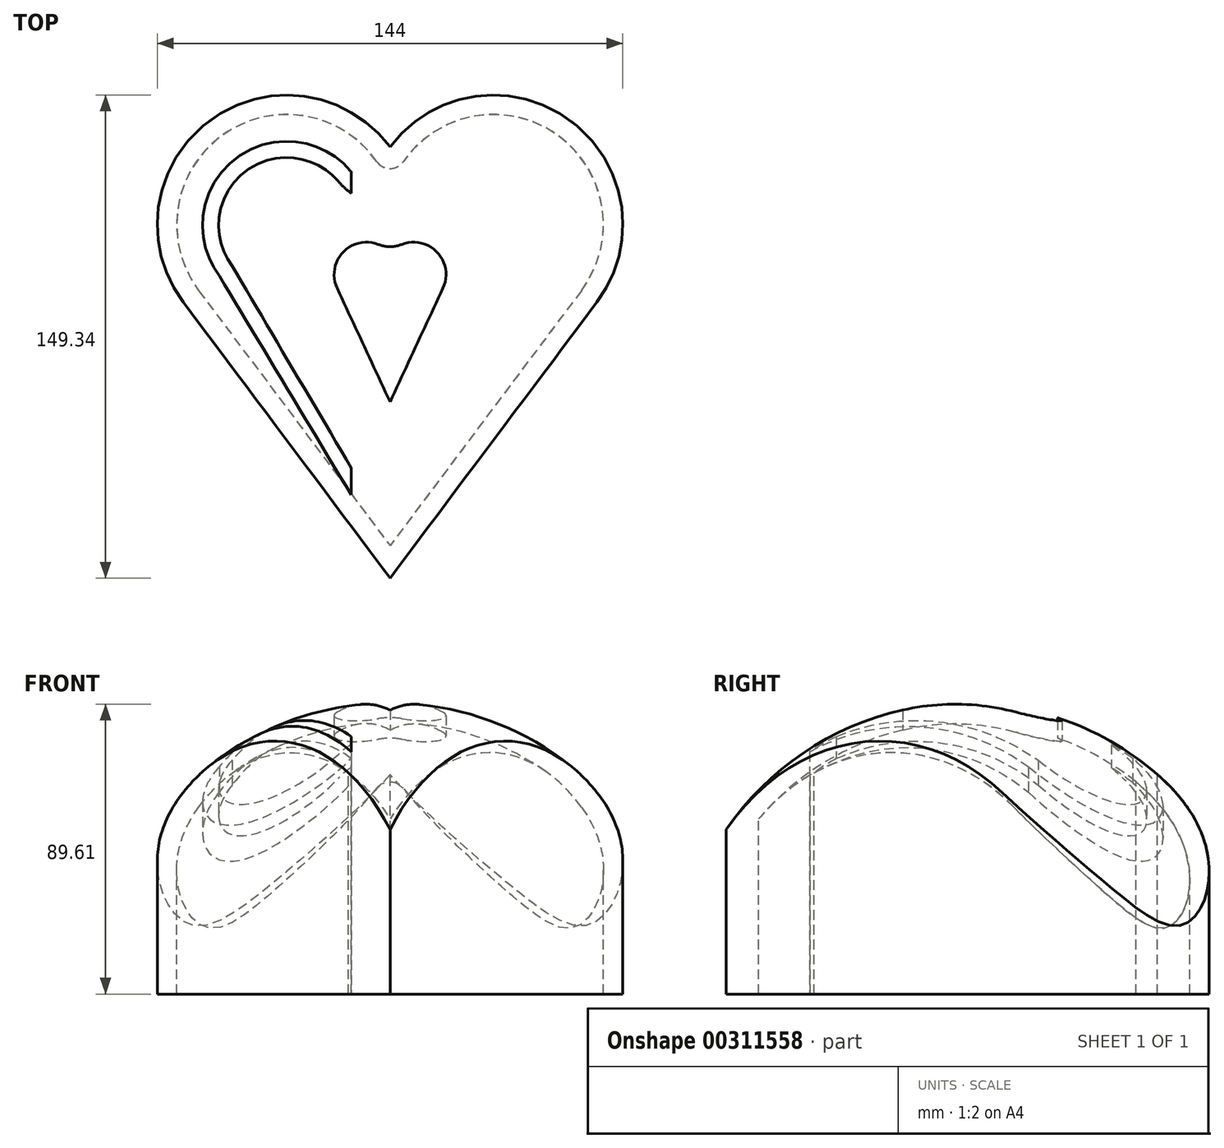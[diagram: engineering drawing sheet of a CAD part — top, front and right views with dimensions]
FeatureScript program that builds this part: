
annotation { "Feature Type Name" : "Feature", "Feature Type Description" : "" }
export const myFeature = defineFeature(function(context is Context, id is Id, definition is map)
    precondition{}
    {
        {
            var Q0;
            Q0=qCreatedBy(makeId("Top.planeOp"),FACE);
            var sketch = newSketch(context, id + "F0", { "sketchPlane" : qUnion([Q0])});
            skArc(sketch, "E0", {"start": v(0, -90) * mm, "mid": v(90, 0) * mm, "end": v(0, 90) * mm});
            skLineSegment(sketch, "E1", {"start": v(0, -90) * mm, "end": v(0, 90) * mm});
            skSolve(sketch);
        }
        {
            var Q0;
            Q0=qCreatedBy(makeId("Top.planeOp"),FACE);
            var sketch = newSketch(context, id + "F1", { "sketchPlane" : qUnion([Q0])});
            skLineSegment(sketch, "E2", {"start": v(0, -74.22) * mm, "end": v(-64, 11.12) * mm});
            skArc(sketch, "E3", {"start": v(0, 59.12) * mm, "mid": v(-56, 67.12) * mm, "end": v(-64, 11.12) * mm});
            skArc(sketch, "E4.MirrorCS", {"start": v(0, 59.12) * mm, "mid": v(56, 67.12) * mm, "end": v(64, 11.12) * mm});
            skLineSegment(sketch, "E5.MirrorCS", {"start": v(0, -74.22) * mm, "end": v(64, 11.12) * mm});
            skPoint(sketch, "E6.orphan", {"position": v(0, 11.12) * mm});
            skCircle(sketch, "E7", {"center": v(0, 0) * mm, "radius": 132.96 * mm});
            skSolve(sketch);
        }
        {
            var Q0;
            Q0=makeQuery(id+"F0.imprint","IMPRINT",FACE,{"disambiguationData":[TD([[makeQuery(id+"F0.imprint","IMPRINT",EDGE,{"derivedFrom":sQuery(id+"F0.wireOp",EDGE,"E0")}),1.0]])]});
            var Q1;
            Q1=sQuery(id+"F0.wireOp",EDGE,"E1");
            revolve(context, id + "F2", {"entities" : qUnion([Q0]), "axis" : qUnion([Q1]), "revolveType" : RevolveType.FULL});
        }
        {
            var Q0;
            Q0=makeQuery(id+"F1.imprint","IMPRINT",FACE,{"disambiguationData":[TD([[makeQuery(id+"F1.imprint","IMPRINT",EDGE,{"derivedFrom":sQuery(id+"F1.wireOp",EDGE,"E2")}),1.0]])]});
            extrude(context, id + "F3", {"entities" : qUnion([Q0]), "operationType" : NewBodyOperationType.REMOVE, "endBound" : BoundingType.SYMMETRIC, "oppositeDirection" : true, "depth" : 255 * mm});
        }
        {
            var Q0;
            Q0=qCreatedBy(makeId("Right.planeOp"),FACE);
            var sketch = newSketch(context, id + "F4", { "sketchPlane" : qUnion([Q0])});
            skLineSegment(sketch, "E8.bottom", {"start": v(92.34, 0) * mm, "end": v(-99.26, 0) * mm});
            skLineSegment(sketch, "E8.top", {"start": v(92.34, -98.37) * mm, "end": v(-99.26, -98.37) * mm});
            skLineSegment(sketch, "E8.left", {"start": v(92.34, 0) * mm, "end": v(92.34, -98.37) * mm});
            skLineSegment(sketch, "E8.right", {"start": v(-99.26, 0) * mm, "end": v(-99.26, -98.37) * mm});
            skSolve(sketch);
        }
        {
            var Q0;
            Q0=makeQuery(id+"F4.imprint","IMPRINT",FACE,{"disambiguationData":[TD([[makeQuery(id+"F4.imprint","IMPRINT",EDGE,{"derivedFrom":sQuery(id+"F4.wireOp",EDGE,"E8.bottom")}),1.0]])]});
            extrude(context, id + "F5", {"entities" : qUnion([Q0]), "operationType" : NewBodyOperationType.REMOVE, "endBound" : BoundingType.SYMMETRIC, "oppositeDirection" : true, "depth" : 202.6 * mm});
        }
        {
            var Q0;
            Q0=makeQuery(id+"F5.boolean.opBoolean","COPY",FACE,{"derivedFrom":makeQuery(id+"F5.opExtrude","SWEPT_FACE",FACE,{"disambiguationData":[OSD([sQuery(id+"F4.wireOp",EDGE,"E8.bottom")])]})});
            shell(context, id + "F6", {"entities" : qUnion([Q0]), "thickness" : 6 * mm});
        }
        {
            var Q0;
            Q0=qCreatedBy(makeId("Top.planeOp"),FACE);
            var sketch = newSketch(context, id + "F7", { "sketchPlane" : qUnion([Q0])});
            skPoint(sketch, "E9.visualSharp", {"position": v(0, 46.32) * mm});
            skArc(sketch, "E10.0", {"start": v(-12.2, 51.67) * mm, "mid": v(-48.23, 55.14) * mm, "end": v(-52.8, 19.23) * mm});
            skLineSegment(sketch, "E10.1", {"start": v(-12, -48.5) * mm, "end": v(-52.8, 19.23) * mm});
            skArc(sketch, "E10.2", {"start": v(-12.2, 51.67) * mm, "mid": v(-12.1, 51.56) * mm, "end": v(-12, 51.45) * mm});
            skArc(sketch, "E10.3", {"start": v(12.2, 51.67) * mm, "mid": v(48.23, 55.14) * mm, "end": v(52.8, 19.23) * mm});
            skLineSegment(sketch, "E10.4", {"start": v(12, -48.5) * mm, "end": v(52.8, 19.23) * mm});
            skArc(sketch, "E11.0", {"start": v(16, 48.43) * mm, "mid": v(45.1, 51.24) * mm, "end": v(48.8, 22.23) * mm});
            skArc(sketch, "E11.1", {"start": v(-16, 48.43) * mm, "mid": v(-14.12, 46.49) * mm, "end": v(-12, 44.8) * mm});
            skArc(sketch, "E11.2", {"start": v(-16, 48.43) * mm, "mid": v(-45.1, 51.24) * mm, "end": v(-48.8, 22.23) * mm});
            skLineSegment(sketch, "E12.trimOffspring", {"start": v(-12, -40.17) * mm, "end": v(-48.8, 22.23) * mm});
            skLineSegment(sketch, "E13.trimOffspring", {"start": v(12, -40.17) * mm, "end": v(48.8, 22.23) * mm});
            skLineSegment(sketch, "E14", {"start": v(-12, -48.5) * mm, "end": v(-12, -40.17) * mm});
            skLineSegment(sketch, "E15.MirrorCS", {"start": v(12, -48.5) * mm, "end": v(12, -40.17) * mm});
            skPoint(sketch, "E16.orphan", {"position": v(-12, -28.45) * mm});
            skPoint(sketch, "E17.orphan", {"position": v(12, -28.45) * mm});
            skPoint(sketch, "E18.orphan", {"position": v(0, -68.42) * mm});
            skPoint(sketch, "E19.orphan", {"position": v(-12, -53.75) * mm});
            skPoint(sketch, "E20.orphan", {"position": v(12, -53.75) * mm});
            skLineSegment(sketch, "E21", {"start": v(-12, 44.8) * mm, "end": v(-12, 51.45) * mm});
            skLineSegment(sketch, "E22.MirrorCS", {"start": v(12, 44.8) * mm, "end": v(12, 51.45) * mm});
            skPoint(sketch, "E23.orphan", {"position": v(-12, 35.9) * mm});
            skArc(sketch, "E24.trimOffspring", {"start": v(12, 44.8) * mm, "mid": v(14.12, 46.49) * mm, "end": v(16, 48.43) * mm});
            skArc(sketch, "E25.trimOffspring", {"start": v(12, 51.45) * mm, "mid": v(12.1, 51.56) * mm, "end": v(12.2, 51.67) * mm});
            skPoint(sketch, "E26.orphan", {"position": v(-12, 54.73) * mm});
            skPoint(sketch, "E27.orphan", {"position": v(12, 54.73) * mm});
            skPoint(sketch, "E28.orphan", {"position": v(12, 35.9) * mm});
            skSolve(sketch);
        }
        {
            var Q0;
            Q0=makeQuery(id+"F7.imprint","IMPRINT",FACE,{"disambiguationData":[TD([[makeQuery(id+"F7.imprint","IMPRINT",EDGE,{"derivedFrom":sQuery(id+"F7.wireOp",EDGE,"E10.0")}),1.0]])]});
            var Q1;
            Q1=makeQuery(id+"F7.imprint","IMPRINT",FACE,{"disambiguationData":[TD([[makeQuery(id+"F7.imprint","IMPRINT",EDGE,{"derivedFrom":sQuery(id+"F7.wireOp",EDGE,"E10.3")}),-1.0]])]});
            extrude(context, id + "F8", {"entities" : qUnion([Q0, Q1]), "operationType" : NewBodyOperationType.REMOVE, "depth" : 119.5 * mm});
        }
        {
            var Q0;
            Q0=qCreatedBy(makeId("Top.planeOp"),FACE);
            var sketch = newSketch(context, id + "F9", { "sketchPlane" : qUnion([Q0])});
            skPoint(sketch, "E29.orphan", {"position": v(13.76, -32.3) * mm});
            skArc(sketch, "E30.0", {"start": v(-3.65, 28.95) * mm, "mid": v(-14.59, 26.48) * mm, "end": v(-16.36, 15.41) * mm});
            skLineSegment(sketch, "E30.1", {"start": v(0, -19.7) * mm, "end": v(-16.36, 15.41) * mm});
            skArc(sketch, "E30.2", {"start": v(-3.65, 28.95) * mm, "mid": v(-1.86, 28.43) * mm, "end": v(0, 28.26) * mm});
            skArc(sketch, "E31.MirrorCS", {"start": v(3.65, 28.95) * mm, "mid": v(1.86, 28.43) * mm, "end": v(0, 28.26) * mm});
            skArc(sketch, "E32.MirrorCS", {"start": v(3.65, 28.95) * mm, "mid": v(14.59, 26.48) * mm, "end": v(16.36, 15.41) * mm});
            skLineSegment(sketch, "E33.MirrorCS", {"start": v(0, -19.7) * mm, "end": v(16.36, 15.41) * mm});
            skSolve(sketch);
        }
        {
            var Q0;
            Q0=makeQuery(id+"F9.imprint","IMPRINT",FACE,{"disambiguationData":[TD([[makeQuery(id+"F9.imprint","IMPRINT",EDGE,{"derivedFrom":sQuery(id+"F9.wireOp",EDGE,"E30.0")}),1.0]])]});
            extrude(context, id + "F10", {"entities" : qUnion([Q0]), "operationType" : NewBodyOperationType.REMOVE, "depth" : 145 * mm});
        }
        {
            var Q0;
            Q0=makeQuery(id+"F6.opShell","OFFSET_EDGE",EDGE,{"disambiguationData":[OSD([sQuery(id+"F1.wireOp",EDGE,"E3"),sQuery(id+"F1.wireOp",EDGE,"E4.MirrorCS")])]});
            fillet(context, id + "F11", {"entities" : qUnion([Q0]), "radius" : 5 * mm, "tangentPropagation" : true, "allowEdgeOverflow" : false});
        }
    });
